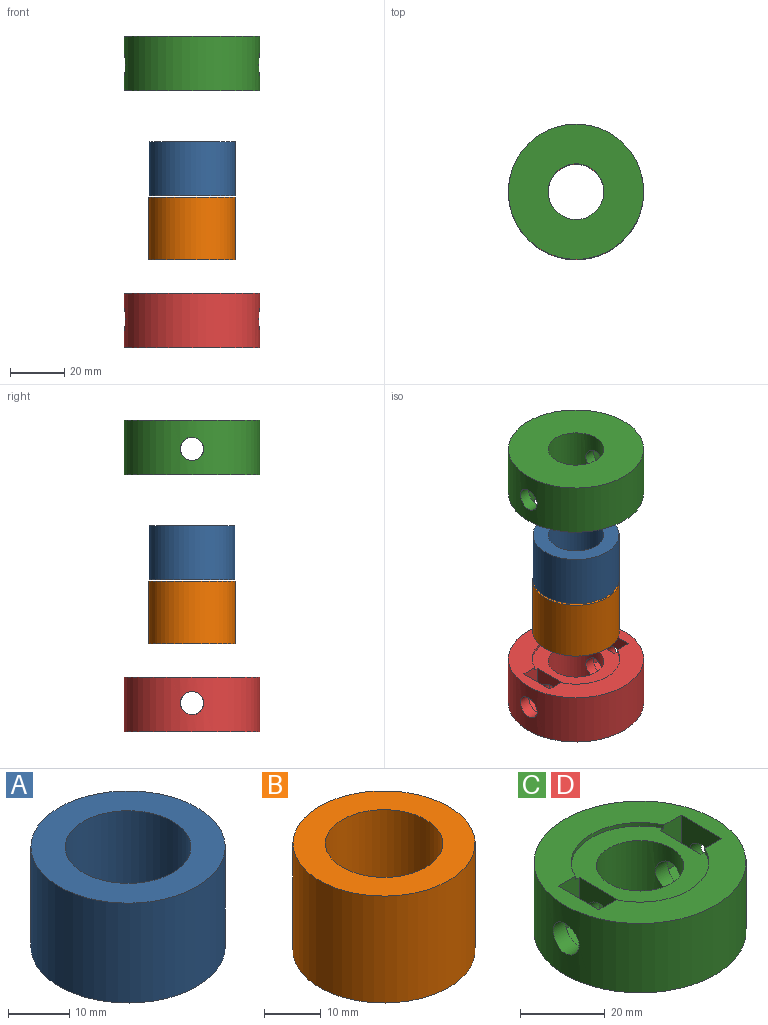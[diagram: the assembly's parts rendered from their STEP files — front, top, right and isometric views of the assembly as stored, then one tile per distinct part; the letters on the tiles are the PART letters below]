
ASSEMBLY  parts=4 mates=3
PART A: 4 faces, bbox 31.8x31.8x20 mm
  f0: cylinder r=10.3mm len=20.6mm, axis (0,0,-1), area 1294.3mm2, adj f2,f3
  f1: cylinder r=15.9mm len=31.8mm, axis (0,0,-1), area 1998.1mm2, adj f2,f3
  f2: plane 31.8x31.8mm, normal (0,0,1), area 460.9mm2, adj f0,f1
  f3: plane 31.8x31.8mm, normal (0,0,-1), area 460.9mm2, adj f0,f1
PART B: 4 faces, bbox 32x32x23 mm
  f0: cylinder r=10.3mm len=23mm, axis (0,0,-1), area 1488.5mm2, adj f2,f3
  f1: cylinder r=16mm len=32mm, axis (0,0,-1), area 2312.2mm2, adj f2,f3
  f2: plane 32x32mm, normal (0,0,1), area 471mm2, adj f0,f1
  f3: plane 32x32mm, normal (0,0,-1), area 471mm2, adj f0,f1
PART C: 23 faces, bbox 50x50x20 mm
  f0: cylinder r=10.3mm len=20.6mm, axis (0,0,-1), area 1110.7mm2, adj f5,f16,f18,f22
  f1: plane 16.5x13.6mm, normal (1,0,0), area 139.6mm2, adj f6,f7,f12,f13,f18,f22
  f2: plane 16.5x13.6mm, normal (-1,0,0), area 139.6mm2, adj f9,f11,f14,f15,f16,f22
  f3: cylinder r=25mm len=50mm, axis (0,0,-1), area 3025mm2, adj f4,f5,f17,f19
  f4: plane 50x50mm, normal (0,0,1), area 1005.1mm2, adj f3,f6,f7,f8,f9,f10,f11,f20
  f5: plane 50x50mm, normal (0,0,-1), area 1630.2mm2, adj f0,f3
  f6: plane 13.57x7mm, normal (0,-1,0), area 93.8mm2, adj f1,f4,f8,f13,f21,f22
  f7: plane 13.57x7mm, normal (0,1,0), area 93.8mm2, adj f1,f4,f8,f12,f20,f22
  f8: plane 17.5x13.6mm, normal (-1,0,0), area 153.2mm2, adj f4,f6,f7,f12,f13,f17
  f9: plane 13.57x7mm, normal (0,-1,0), area 93.8mm2, adj f2,f4,f10,f14,f21,f22
  f10: plane 17.5x13.6mm, normal (1,0,0), area 153.2mm2, adj f4,f9,f11,f14,f15,f19
  f11: plane 13.57x7mm, normal (0,1,0), area 93.8mm2, adj f2,f4,f10,f15,f20,f22
  f12: plane 7x6.8mm, normal (0,0.5,0.87), area 55mm2, adj f1,f7,f8,f13
  f13: plane 7x6.8mm, normal (0,-0.5,0.87), area 55mm2, adj f1,f6,f8,f12
  f14: plane 7x6.8mm, normal (0,-0.5,0.87), area 55mm2, adj f2,f9,f10,f15
  f15: plane 7x6.8mm, normal (0,0.5,0.87), area 55mm2, adj f2,f10,f11,f14
  f16: cylinder r=4.3mm len=8.6mm, axis (-1,0,0), area 99mm2, adj f0,f2
  f17: cylinder r=4.3mm len=8.6mm, axis (-1,0,0), area 116.6mm2, adj f3,f8
  f18: cylinder r=4.3mm len=8.6mm, axis (-1,0,0), area 99mm2, adj f0,f1
  f19: cylinder r=4.3mm len=8.6mm, axis (1,0,0), area 116.6mm2, adj f3,f10
  f20: cylinder r=16.25mm len=29.52mm, axis (0,0,1), area 37mm2, adj f4,f7,f11,f22
  f21: cylinder r=16.25mm len=29.52mm, axis (0,0,1), area 37mm2, adj f4,f6,f9,f22
  f22: plane 32.5x29.52mm, normal (0,0,1), area 434.7mm2, adj f0,f1,f2,f6,f7,f9,f11,f20
PART D: same geometry as C
PLACE A rot(axis=(1,0,0),180deg) t=(-51.39,-83.87,-11.15)mm
PLACE B t=(-51.39,-83.87,-54.77)mm
PLACE C rot(axis=(1,0,0),180deg) t=(-51.39,-83.87,27.68)mm
PLACE D t=(-51.39,-83.87,-87.28)mm
MATE slider A.f0 <-> C.f3  axis (0,0,-1) through (-51.39,-83.87,-31.15)mm
MATE slider B.f0 <-> D.f0  axis (0,0,1) through (-51.39,-83.87,-31.77)mm
MATE slider B.f0 <-> C.f3  axis (0,0,1) through (-51.39,-83.87,-31.77)mm
